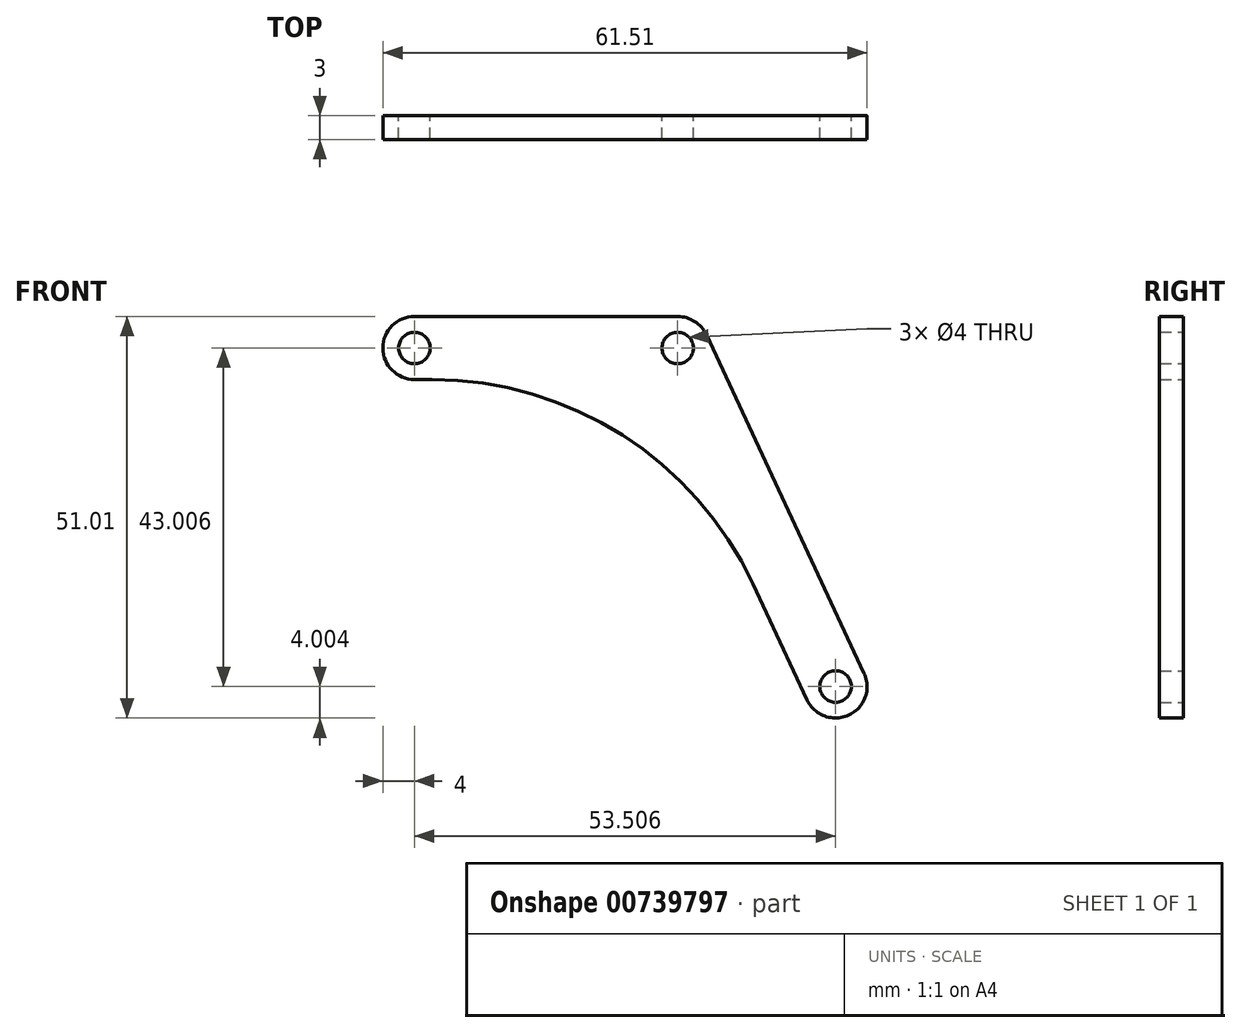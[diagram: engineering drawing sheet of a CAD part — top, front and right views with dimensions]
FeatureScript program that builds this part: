
annotation { "Feature Type Name" : "Feature", "Feature Type Description" : "" }
export const myFeature = defineFeature(function(context is Context, id is Id, definition is map)
    precondition{}
    {
        {
            var Q0;
            Q0=qCreatedBy(makeId("Front.planeOp"),FACE);
            var sketch = newSketch(context, id + "F0", { "sketchPlane" : qUnion([Q0])});
            skLineSegment(sketch, "E0", {"start": v(-2.55, 0) * mm, "end": v(-36, 0) * mm});
            skLineSegment(sketch, "E1", {"start": v(-36, 0) * mm, "end": v(-36, -8) * mm, "construction": true});
            skLineSegment(sketch, "E2", {"start": v(-36, -8) * mm, "end": v(-33.76, -8) * mm});
            skLineSegment(sketch, "E3", {"start": v(7.02, -33.98) * mm, "end": v(13.88, -48.7) * mm});
            skLineSegment(sketch, "E4", {"start": v(13.88, -48.7) * mm, "end": v(21.13, -45.32) * mm, "construction": true});
            skLineSegment(sketch, "E5", {"start": v(21.13, -45.32) * mm, "end": v(1.08, -2.3) * mm});
            skArc(sketch, "E6", {"start": v(-36, 0) * mm, "mid": v(-40, -4) * mm, "end": v(-36, -8) * mm});
            skArc(sketch, "E7", {"start": v(13.88, -48.7) * mm, "mid": v(19.2, -50.63) * mm, "end": v(21.13, -45.32) * mm});
            skPoint(sketch, "E8.visualSharp", {"position": v(-5.1, -8) * mm});
            skArc(sketch, "E8.filletArc", {"start": v(7.02, -33.98) * mm, "mid": v(-9.59, -15.05) * mm, "end": v(-33.76, -8) * mm});
            skPoint(sketch, "E9.visualSharp", {"position": v(0, 0) * mm});
            skArc(sketch, "E9.filletArc", {"start": v(1.08, -2.3) * mm, "mid": v(-0.4, -0.63) * mm, "end": v(-2.55, 0) * mm});
            skCircle(sketch, "E10", {"center": v(-36, -4) * mm, "radius": 2 * mm});
            skCircle(sketch, "E11", {"center": v(-2.55, -4) * mm, "radius": 2 * mm});
            skCircle(sketch, "E12", {"center": v(17.5, -47) * mm, "radius": 2 * mm});
            skSolve(sketch);
        }
        {
            var Q0;
            Q0 = qSketchRegion(id + "F0", true);
            extrude(context, id + "F1", {"entities" : qUnion([Q0]), "depth" : 3 * mm, "offsetDistance" : 25 * mm});
        }
    });
